# Revit family: JC KONTAKTER JCK108 Armbågskontakt
name_source: partatom
category: Specialty Equipment
units: mm (PartAtom-declared; Revit-internal decimal feet)

## family parameters
Always vertical = Yes
Cut with Voids When Loaded = No
Enable Cutting in Views = Yes
Host = Wall
Maintain Annotation Orientation = No
Part Type = Normal
Room Calculation Point = No
Round Connector Dimension = Use Diameter
Shared = No

## types (2) — shared parameters
Antal mikrobrytare = 2
CE Dokument = https://jckontakter.se
Core Finish = Aluminum ENAW 6060
Description = JCK108 är en robust armbågskontakt i aluminium. Modellen har en konkav tryckplatta med kontrasterande svarta endcaps och är speciellt lämplig att installeras i krävande miljöer.
JCK108 levereras med 2st mikrobrytare i IP67.
End Cap Finish = POM Tenac C 4520
Lid Finish = Aluminum ENAW 6060
Lägsta märkström = 1mA/4 V DC
Manufacturer = JC Kontakter
Mikrobrytare = Standard NO IP67
Model = JCK108
Nominell märkström = 0,1A - 10 A/250 V AC
Placering av armbågskontakt = https://jckontakter.se
Tekniskt produktblad = https://jckontakter.se
Tillvalsförteckning = https://jckontakter.se
Tillverkningsland = Sverige
URL = https://jckontakter.se
zero-valued in all types: Default Elevation

## per-type parameters (varying)
| type | Produktvikt |
| Type 1 | 0.305 kg |
| Armbågskontakt JCK108 | 0.416 kg |

## geometry (parser evidence)
native form markers: Sweep x5
no freeform markers — native parametric forms only
